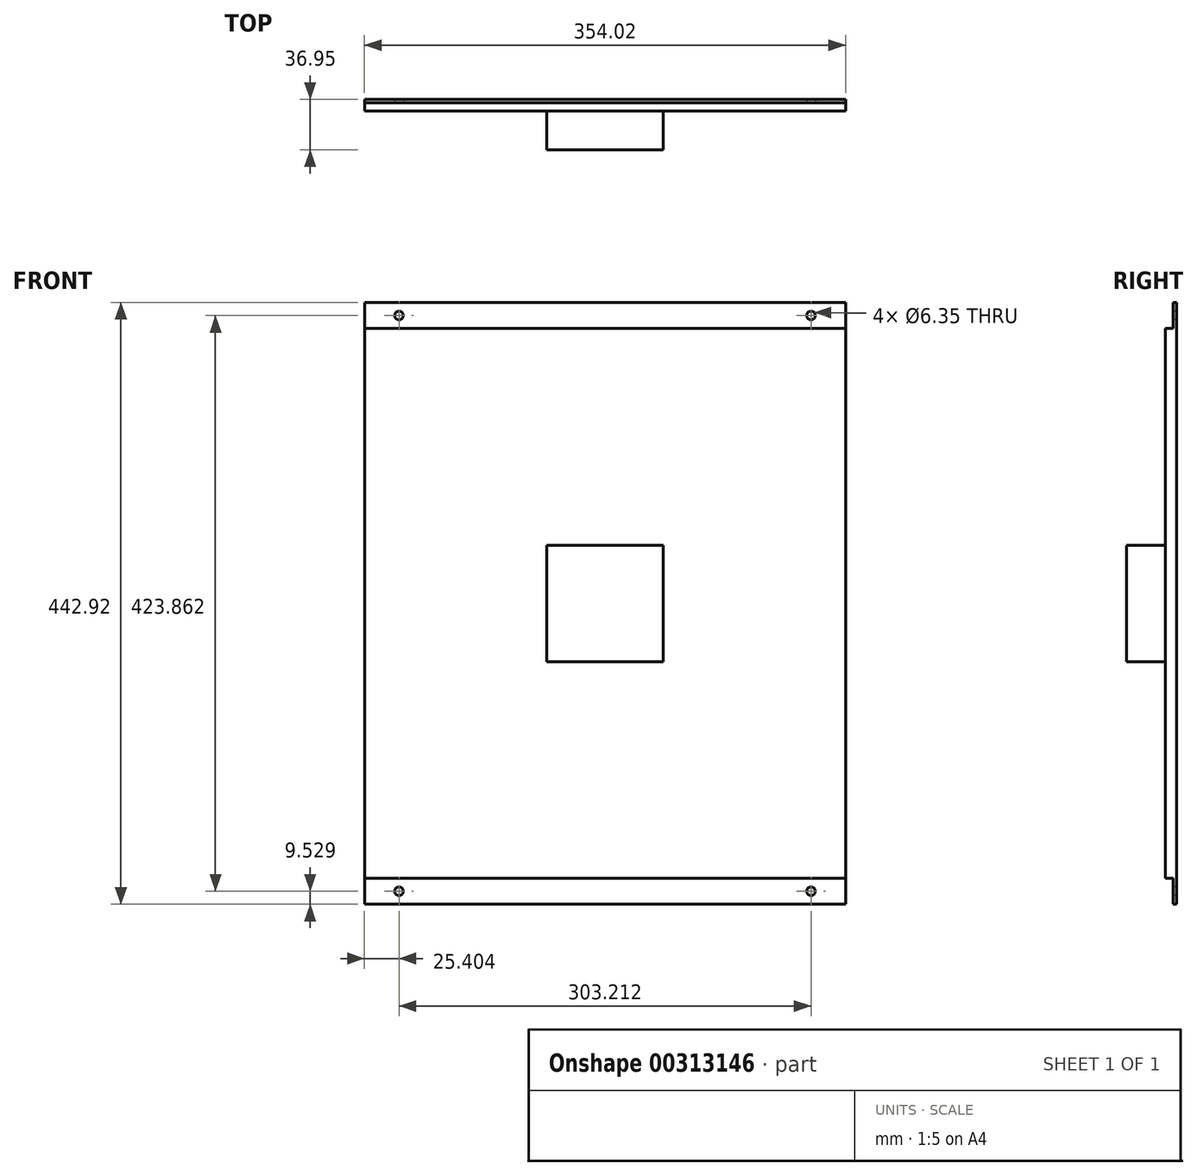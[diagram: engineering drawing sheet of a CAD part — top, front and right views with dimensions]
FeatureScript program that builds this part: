
annotation { "Feature Type Name" : "Feature", "Feature Type Description" : "" }
export const myFeature = defineFeature(function(context is Context, id is Id, definition is map)
    precondition{}
    {
        {
            var Q0;
            Q0=qCreatedBy(makeId("Front.planeOp"),FACE);
            var sketch = newSketch(context, id + "F0", { "sketchPlane" : qUnion([Q0])});
            skLineSegment(sketch, "E0.bottom", {"start": v(177, 202.4) * mm, "end": v(-177, 202.4) * mm});
            skLineSegment(sketch, "E0.top", {"start": v(177, -202.4) * mm, "end": v(-177, -202.4) * mm});
            skLineSegment(sketch, "E0.left", {"start": v(177, 202.4) * mm, "end": v(177, -202.4) * mm});
            skLineSegment(sketch, "E0.right", {"start": v(-177, 202.4) * mm, "end": v(-177, -202.4) * mm});
            skPoint(sketch, "E0.middle", {"position": v(0, 0) * mm});
            skSolve(sketch);
        }
        {
            var Q0;
            Q0 = qSketchRegion(id + "F0", true);
            extrude(context, id + "F1", {"entities" : qUnion([Q0]), "endBound" : BoundingType.SYMMETRIC, "depth" : (8 + (3 / 8)) * mm, "offsetDistance" : 25.4 * mm});
        }
        {
            var Q0;
            Q0=makeQuery(id+"F1.opExtrude","CAP_FACE",FACE,{"disambiguationData":[OSD([sQuery(id+"F0.wireOp",EDGE,"E0.bottom"),sQuery(id+"F0.wireOp",EDGE,"E0.top"),sQuery(id+"F0.wireOp",EDGE,"E0.left"),sQuery(id+"F0.wireOp",EDGE,"E0.right")])],"isStart":false});
            var sketch = newSketch(context, id + "F2", { "sketchPlane" : qUnion([Q0])});
            skLineSegment(sketch, "E1.bottom", {"start": v(42.86, 42.86) * mm, "end": v(-42.86, 42.86) * mm});
            skLineSegment(sketch, "E1.top", {"start": v(42.86, -42.86) * mm, "end": v(-42.86, -42.86) * mm});
            skLineSegment(sketch, "E1.left", {"start": v(42.86, 42.86) * mm, "end": v(42.86, -42.86) * mm});
            skLineSegment(sketch, "E1.right", {"start": v(-42.86, 42.86) * mm, "end": v(-42.86, -42.86) * mm});
            skPoint(sketch, "E1.middle", {"position": v(0, 0) * mm});
            skSolve(sketch);
        }
        {
            var Q0;
            Q0 = qSketchRegion(id + "F2", true);
            extrude(context, id + "F3", {"entities" : qUnion([Q0]), "operationType" : NewBodyOperationType.ADD, "depth" : 28.57 * mm});
        }
        {
            var Q0;
            Q0=makeQuery(id+"F1.opExtrude","CAP_FACE",FACE,{"disambiguationData":[OSD([sQuery(id+"F0.wireOp",EDGE,"E0.bottom"),sQuery(id+"F0.wireOp",EDGE,"E0.top"),sQuery(id+"F0.wireOp",EDGE,"E0.left"),sQuery(id+"F0.wireOp",EDGE,"E0.right")])],"isStart":true});
            var sketch = newSketch(context, id + "F4", { "sketchPlane" : qUnion([Q0])});
            skLineSegment(sketch, "E2.bottom", {"start": v(177, 221.46) * mm, "end": v(-177, 221.46) * mm});
            skLineSegment(sketch, "E2.top", {"start": v(177, -221.46) * mm, "end": v(-177, -221.46) * mm});
            skLineSegment(sketch, "E2.left", {"start": v(177, 221.46) * mm, "end": v(177, -221.46) * mm});
            skLineSegment(sketch, "E2.right", {"start": v(-177, 221.46) * mm, "end": v(-177, -221.46) * mm});
            skPoint(sketch, "E2.middle", {"position": v(0, 0) * mm});
            skSolve(sketch);
        }
        {
            var Q0;
            Q0 = qSketchRegion(id + "F4", true);
            extrude(context, id + "F5", {"entities" : qUnion([Q0]), "operationType" : NewBodyOperationType.ADD, "oppositeDirection" : true, "depth" : 2.54 * mm});
        }
        {
            var Q0;
            {var subQ0=sQuery(id+"F4.wireOp",EDGE,"E2.bottom");var subQ1=sQuery(id+"F4.wireOp",EDGE,"E2.right");var subQ2=sQuery(id+"F4.wireOp",EDGE,"E2.left");Q0=makeQuery(id+"F5.boolean.opBoolean","SPLIT",FACE,{"disambiguationData":[TD([makeQuery(id+"F1.opExtrude","SWEPT_FACE",FACE,{"disambiguationData":[OSD([sQuery(id+"F0.wireOp",EDGE,"E0.bottom")])]})])],"derivedFrom":makeQuery(id+"F5.opExtrude","CAP_FACE",FACE,{"disambiguationData":[OSD([subQ0,sQuery(id+"F4.wireOp",EDGE,"E2.top"),subQ2,subQ1])],"isStart":false})});}
            var sketch = newSketch(context, id + "F6", { "sketchPlane" : qUnion([Q0])});
            skCircle(sketch, "E3", {"center": v(-151.6, 211.93) * mm, "radius": 3.17 * mm});
            skCircle(sketch, "E4", {"center": v(151.6, 211.93) * mm, "radius": 3.17 * mm});
            skCircle(sketch, "E5", {"center": v(151.6, -211.93) * mm, "radius": 3.17 * mm});
            skCircle(sketch, "E6", {"center": v(-151.6, -211.93) * mm, "radius": 3.17 * mm});
            skSolve(sketch);
        }
        {
            var Q0;
            Q0 = qSketchRegion(id + "F6", true);
            extrude(context, id + "F7", {"entities" : qUnion([Q0]), "operationType" : NewBodyOperationType.REMOVE, "endBound" : BoundingType.THROUGH_ALL, "oppositeDirection" : true, "depth" : 25.4 * mm});
        }
    });
